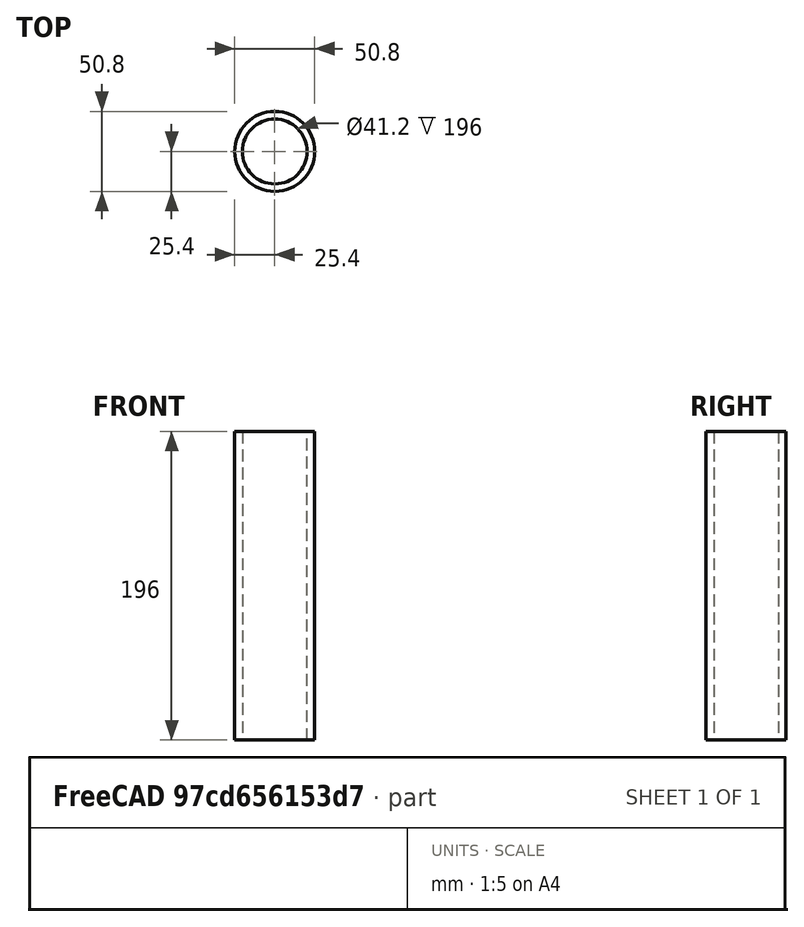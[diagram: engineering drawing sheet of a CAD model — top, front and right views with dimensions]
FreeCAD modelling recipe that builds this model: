
FCSTD DOCUMENT  (FreeCAD 0.19R24267 +99 (Git))
Label: Steel tube spacer 196mm length
License: All rights reserved
LicenseURL: http://en.wikipedia.org/wiki/All_rights_reserved
objects: Sketcher::SketchObject×1, PartDesign::Pad×1, PartDesign::Body×1
note: 4 computed .brp shape members not serialized (recipe doc carries the construction recipe); baked Part::Feature solids carry a one-line shape summary decoded from their .brp

FEATURE [Sketcher::SketchObject] Sketch  label="Cross section"
  FullyConstrained = true
  MapMode = 5
  Support = -> [XY_Plane]
  sketch-geometry (4):
    g0: Circle CenterX=0 CenterY=0 CenterZ=0 NormalX=0 NormalY=0 NormalZ=1 AngleXU=0 Radius=20.6
    g1: Circle CenterX=0 CenterY=0 CenterZ=0 NormalX=0 NormalY=0 NormalZ=1 AngleXU=0 Radius=25.4
    g2: GeomPoint X=20.6 Y=0 Z=0
    g3: GeomPoint X=25.4 Y=0 Z=0
  constraints (8):
    c: Coincident(g0,g-1)
    c: Coincident(g1,g0)
    c: PointOnObject(g2,g0)
    c: PointOnObject(g3,g1)
    c: PointOnObject(g3,g-1)
    c: PointOnObject(g2,g-1)
    c: DistanceX(g2,g3) = 4.8
    c: Diameter(g1) = 50.8
FEATURE [PartDesign::Pad] Pad  label="Length"
  Direction = (1,1,1)
  Length = 196
  Length2 = 100
  Profile = -> Sketch
  Type = 0
FEATURE [PartDesign::Body] Body
  Group = -> [Sketch,Pad]
  Origin = -> Origin
  Tip = -> Pad
